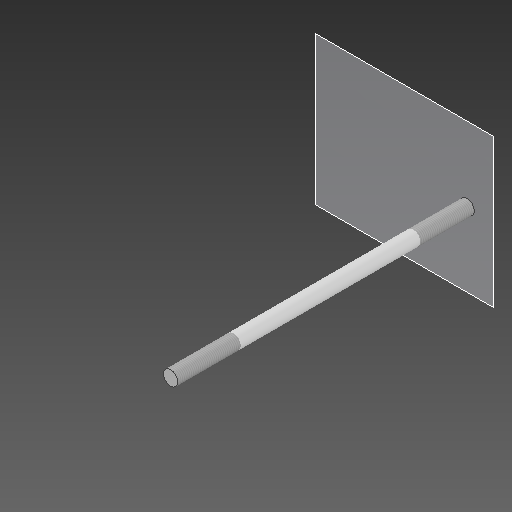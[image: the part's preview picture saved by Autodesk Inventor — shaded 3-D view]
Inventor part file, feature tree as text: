
AUTODESK INVENTOR PART (.ipt)
format: ipt  version: 2021 (Build 250183000, 183)  size: 84,992 bytes
history: native  units: in
note: dims shown in document units (in); Inventor stores cm internally (conversion verified against a paired STEP export)
features: other x3, sketch x1, plane x1
ambient origin geometry x8: Origin, YZ Plane, XZ Plane, XY Plane, X Axis, Y Axis, Z Axis, Center Point
bodies: Solid1 (feature_tree)
feature tree (5):
  other  "Eje roscado base soporte tubo.ipt"
  other  "Solid1::Eje roscado base soporte tubo.ipt"
  other  "TaggingFeature1"
  sketch  "Sketch1"  dims[d0=0.3937in]
  plane  "Work Plane1"
